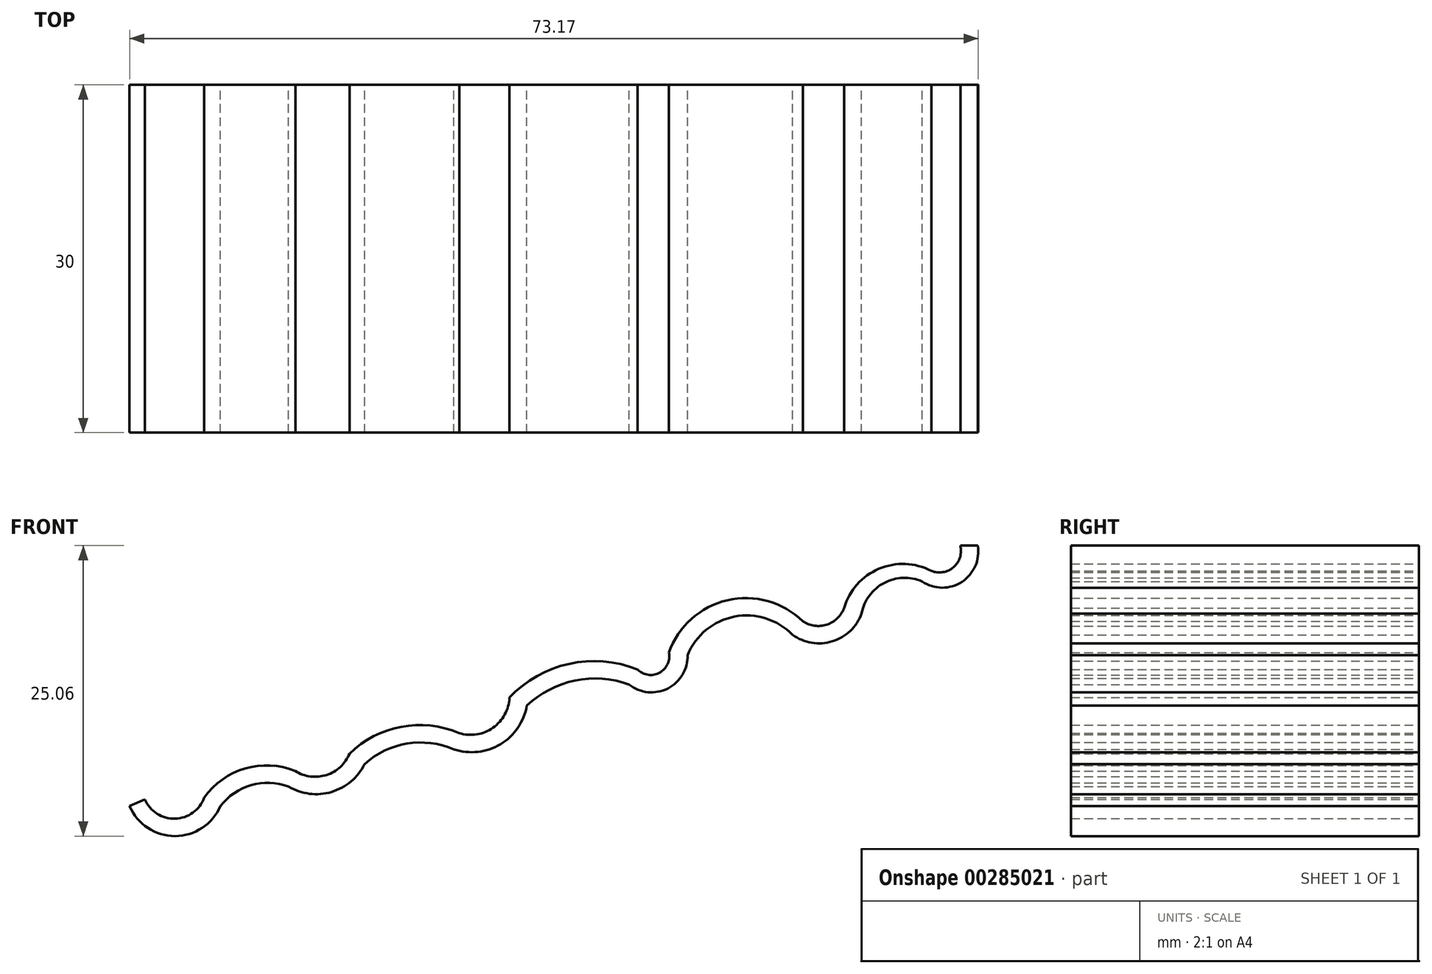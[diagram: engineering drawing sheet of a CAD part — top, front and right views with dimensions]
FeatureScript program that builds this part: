
annotation { "Feature Type Name" : "Feature", "Feature Type Description" : "" }
export const myFeature = defineFeature(function(context is Context, id is Id, definition is map)
    precondition{}
    {
        {
            var Q0;
            Q0=qCreatedBy(makeId("Front.planeOp"),FACE);
            var sketch = newSketch(context, id + "F0", { "sketchPlane" : qUnion([Q0])});
            skLineSegment(sketch, "E0", {"start": v(-1477.5, -539.8) * mm, "end": v(522.5, -539.8) * mm, "construction": true});
            skLineSegment(sketch, "E1", {"start": v(522.5, -539.8) * mm, "end": v(522.5, -39.8) * mm, "construction": true});
            skLineSegment(sketch, "E2", {"start": v(-1477.5, -539.8) * mm, "end": v(-1477.5, -39.8) * mm, "construction": true});
            skLineSegment(sketch, "E3", {"start": v(-1477.5, -39.8) * mm, "end": v(522.5, -39.8) * mm, "construction": true});
            skArc(sketch, "E4", {"start": v(166.26, -101.87) * mm, "mid": v(100.7, -104.05) * mm, "end": v(61.7, -156.78) * mm});
            skArc(sketch, "E5", {"start": v(-57.3, -193.61) * mm, "mid": v(11.4, -204.95) * mm, "end": v(61.7, -156.78) * mm});
            skArc(sketch, "E6", {"start": v(-57.3, -193.61) * mm, "mid": v(-157.33, -162.3) * mm, "end": v(-238.53, -228.57) * mm});
            skArc(sketch, "E7", {"start": v(-339.2, -279.5) * mm, "mid": v(-272.53, -286.32) * mm, "end": v(-238.53, -228.57) * mm});
            skArc(sketch, "E8", {"start": v(-339.2, -279.5) * mm, "mid": v(-432.48, -272.58) * mm, "end": v(-515.4, -315.87) * mm});
            skArc(sketch, "E9", {"start": v(-641.26, -391.38) * mm, "mid": v(-561.03, -382.45) * mm, "end": v(-515.4, -315.87) * mm});
            skArc(sketch, "E10", {"start": v(-641.26, -391.38) * mm, "mid": v(-721.87, -381.38) * mm, "end": v(-795.08, -416.55) * mm});
            skArc(sketch, "E11", {"start": v(-926.54, -455.7) * mm, "mid": v(-852.28, -464.76) * mm, "end": v(-795.08, -416.55) * mm});
            skArc(sketch, "E12", {"start": v(-926.54, -455.7) * mm, "mid": v(-990.83, -453.05) * mm, "end": v(-1044, -489.27) * mm});
            skArc(sketch, "E13", {"start": v(-1200.63, -489.27) * mm, "mid": v(-1122.32, -541.02) * mm, "end": v(-1044, -489.27) * mm});
            skArc(sketch, "E14", {"start": v(166.26, -101.87) * mm, "mid": v(234.57, -102.35) * mm, "end": v(262.03, -39.8) * mm});
            skArc(sketch, "E15.1", {"start": v(-632.22, -363.25) * mm, "mid": v(-732.19, -352.47) * mm, "end": v(-821.44, -398.75) * mm});
            skArc(sketch, "E15.2", {"start": v(-914.64, -428.73) * mm, "mid": v(-861, -435.6) * mm, "end": v(-821.44, -398.75) * mm});
            skArc(sketch, "E15.3", {"start": v(-914.64, -428.73) * mm, "mid": v(-1001.24, -424.4) * mm, "end": v(-1071.94, -474.6) * mm});
            skArc(sketch, "E15.4", {"start": v(-1174.28, -478.04) * mm, "mid": v(-1121.94, -510.98) * mm, "end": v(-1071.94, -474.6) * mm});
            skArc(sketch, "E15.5", {"start": v(-632.22, -363.25) * mm, "mid": v(-573.82, -354.03) * mm, "end": v(-545.52, -302.12) * mm});
            skArc(sketch, "E15.6", {"start": v(-324.88, -253.44) * mm, "mid": v(-442.7, -243.77) * mm, "end": v(-545.52, -302.12) * mm});
            skArc(sketch, "E15.7", {"start": v(-324.88, -253.44) * mm, "mid": v(-287, -259.26) * mm, "end": v(-270.6, -224.63) * mm});
            skArc(sketch, "E15.8", {"start": v(-39.45, -170.52) * mm, "mid": v(-169.9, -134) * mm, "end": v(-270.6, -224.63) * mm});
            skArc(sketch, "E15.9", {"start": v(-39.45, -170.52) * mm, "mid": v(1.62, -176.1) * mm, "end": v(31.65, -147.54) * mm});
            skArc(sketch, "E15.10", {"start": v(181.99, -83.46) * mm, "mid": v(91.6, -79.76) * mm, "end": v(31.65, -147.54) * mm});
            skLineSegment(sketch, "E16", {"start": v(-1174.28, -478.04) * mm, "end": v(-1200.63, -489.27) * mm});
            skArc(sketch, "E17", {"start": v(181.99, -83.46) * mm, "mid": v(220.33, -76.9) * mm, "end": v(232.03, -39.8) * mm});
            skLineSegment(sketch, "E18", {"start": v(232.03, -39.8) * mm, "end": v(262.03, -39.8) * mm});
            skSolve(sketch);
        }
        {
            var Q0;
            Q0=makeQuery(id+"F0.imprint","IMPRINT",FACE,{"disambiguationData":[TD([[makeQuery(id+"F0.imprint","IMPRINT",EDGE,{"derivedFrom":sQuery(id+"F0.wireOp",EDGE,"E4")}),-1.0]])]});
            extrude(context, id + "F1", {"entities" : qUnion([Q0]), "depth" : 600 * mm});
        }
        {
            var Q0;
            Q0=makeQuery(id+"F1.opExtrude","SWEPT_BODY",BODY,{"disambiguationData":[OSD([sQuery(id+"F0.wireOp",EDGE,"E4"),sQuery(id+"F0.wireOp",EDGE,"E5"),sQuery(id+"F0.wireOp",EDGE,"E6"),sQuery(id+"F0.wireOp",EDGE,"E7"),sQuery(id+"F0.wireOp",EDGE,"E8"),sQuery(id+"F0.wireOp",EDGE,"E9"),sQuery(id+"F0.wireOp",EDGE,"E10"),sQuery(id+"F0.wireOp",EDGE,"E11"),sQuery(id+"F0.wireOp",EDGE,"E12"),sQuery(id+"F0.wireOp",EDGE,"E13"),sQuery(id+"F0.wireOp",EDGE,"E14"),sQuery(id+"F0.wireOp",EDGE,"E15.1"),sQuery(id+"F0.wireOp",EDGE,"E15.2"),sQuery(id+"F0.wireOp",EDGE,"E15.3"),sQuery(id+"F0.wireOp",EDGE,"E15.4"),sQuery(id+"F0.wireOp",EDGE,"E15.5"),sQuery(id+"F0.wireOp",EDGE,"E15.6"),sQuery(id+"F0.wireOp",EDGE,"E15.7"),sQuery(id+"F0.wireOp",EDGE,"E15.8"),sQuery(id+"F0.wireOp",EDGE,"E15.9"),sQuery(id+"F0.wireOp",EDGE,"E15.10"),sQuery(id+"F0.wireOp",EDGE,"E16"),sQuery(id+"F0.wireOp",EDGE,"E17"),sQuery(id+"F0.wireOp",EDGE,"E18")])]});
            var Q1;
            Q1=makeQuery(id+"F1.opExtrude","CAP_VERTEX",VERTEX,{"disambiguationData":[OSD([sQuery(id+"F0.wireOp",EDGE,"E14"),sQuery(id+"F0.wireOp",EDGE,"E18")])],"isStart":false});
            transform(context, id + "F2", {"entities" : qUnion([Q0]), "transformType" : TransformType.SCALE_UNIFORMLY, "scale" : 0.05, "scalePoint" : qUnion([Q1]), "makeCopy" : false});
        }
    });
